# Revit family: Light-LED_Pendant-DXV-Modulus-D19070000_Series
name_source: partatom
category: Lighting Fixtures
revit_build: Autodesk Revit 2014 (Build: 20130308_1515(x64)
units: mm (PartAtom-declared; Revit-internal decimal feet)

## types (4) — shared parameters
Apparent Load = 120 VA
Assembly Code = D5020200
Color Filter = 16777215
Description = DXV Modulus LED Pendant Light
Dimming Lamp Color Temperature Shift = <None>
Height = 14 1/2"
Installation Type = Ceiling Mounted
Light Source Symbol Length = 120"
Manufacturer = DXV
Product Page URL = https://www.dxv.com
Spot Beam Angle = 45.00°
Spot Field Angle = 60.00°
Tilt Angle = 90.00°
Type Comments = Adjustable cord length between 4" (102mm) Min. to 72 (1829mm) Max.
URL = https://www.dxv.com
Voltage = 120 V
Wattage Comments = 10w, 3000k, 850 lumens, 120v.
Width = 6"

## per-type parameters (varying)
| type | Finish | Material |
| D19070000.243 | Metal-DXV-243-Matte Black | Metal-DXV-243-Matte Black |
| D19070000.100 | Metal-DXV-100-Polished Chrome | Metal-DXV-100-Polished Chrome |
| D19070000.144 | Metal-DXV-144-Brushed Nickel | Metal-DXV-144-Brushed Nickel |
| D19070000.150 | Metal-DXV-150-Platinum Nickel | Metal-DXV-150-Platinum Nickel |

note: column(s) folded — value = type name in every type: Model

## geometry (parser evidence)
native form markers: Sweep x1
no freeform markers — native parametric forms only
